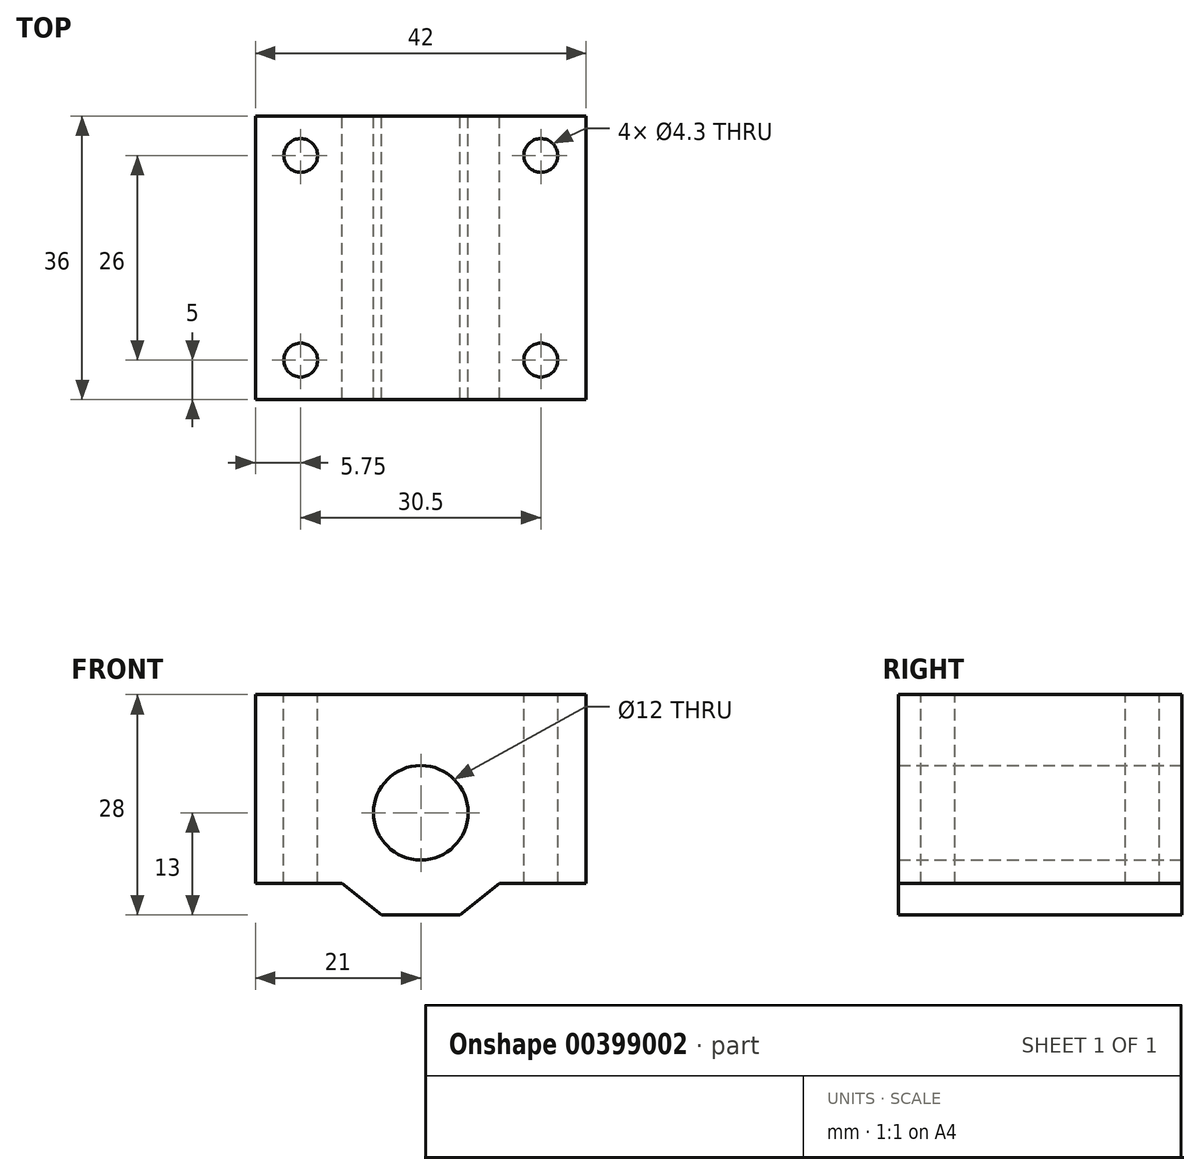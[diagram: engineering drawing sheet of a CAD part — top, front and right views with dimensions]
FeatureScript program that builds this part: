
annotation { "Feature Type Name" : "Feature", "Feature Type Description" : "" }
export const myFeature = defineFeature(function(context is Context, id is Id, definition is map)
    precondition{}
    {
        {
            var Q0;
            Q0=qCreatedBy(makeId("Front.planeOp"),FACE);
            var sketch = newSketch(context, id + "F0", { "sketchPlane" : qUnion([Q0])});
            skCircle(sketch, "E0", {"center": v(0, 0) * mm, "radius": 6 * mm});
            skLineSegment(sketch, "E1.bottom", {"start": v(-21, 15) * mm, "end": v(21, 15) * mm});
            skLineSegment(sketch, "E1.top", {"start": v(-21, -9) * mm, "end": v(-10, -9) * mm});
            skLineSegment(sketch, "E1.left", {"start": v(-21, 15) * mm, "end": v(-21, -9) * mm});
            skLineSegment(sketch, "E1.right", {"start": v(21, 15) * mm, "end": v(21, -9) * mm});
            skLineSegment(sketch, "E2", {"start": v(-10, -9) * mm, "end": v(-5, -13) * mm});
            skLineSegment(sketch, "E3", {"start": v(-5, -13) * mm, "end": v(0, -13) * mm});
            skLineSegment(sketch, "E4.MirrorCS", {"start": v(5, -13) * mm, "end": v(0, -13) * mm});
            skLineSegment(sketch, "E5.MirrorCS", {"start": v(10, -9) * mm, "end": v(5, -13) * mm});
            skLineSegment(sketch, "E6.trimOffspring", {"start": v(10, -9) * mm, "end": v(21, -9) * mm});
            skSolve(sketch);
        }
        {
            var Q0;
            Q0=makeQuery(id+"F0.imprint","IMPRINT",FACE,{"disambiguationData":[TD([[makeQuery(id+"F0.imprint","IMPRINT",EDGE,{"derivedFrom":sQuery(id+"F0.wireOp",EDGE,"E0")}),-1.0]])]});
            extrude(context, id + "F1", {"entities" : qUnion([Q0]), "depth" : 36 * mm, "hasSecondDirection" : true, "secondDirectionOppositeDirection" : true, "secondDirectionDepth" : 18 * mm, "symmetric" : true});
        }
        {
            var Q0;
            Q0=makeQuery(id+"F1.opExtrude","SWEPT_FACE",FACE,{"disambiguationData":[OSD([sQuery(id+"F0.wireOp",EDGE,"E1.bottom")])]});
            var sketch = newSketch(context, id + "F2", { "sketchPlane" : qUnion([Q0])});
            skPoint(sketch, "E7", {"position": v(-15.25, 13) * mm});
            skPoint(sketch, "E8.MirrorP", {"position": v(15.25, 13) * mm});
            skPoint(sketch, "E9.MirrorP", {"position": v(-15.25, -13) * mm});
            skPoint(sketch, "E10.MirrorP", {"position": v(15.25, -13) * mm});
            skSolve(sketch);
        }
        {
            var Q0;
            Q0=sQuery(id+"F2.wireOp",VERTEX,"E7");
            var Q1;
            Q1=sQuery(id+"F2.wireOp",VERTEX,"E8.MirrorP");
            var Q2;
            Q2=sQuery(id+"F2.wireOp",VERTEX,"E10.MirrorP");
            var Q3;
            Q3=sQuery(id+"F2.wireOp",VERTEX,"E9.MirrorP");
            var Q4;
            Q4=makeQuery(id+"F1.opExtrude","SWEPT_BODY",BODY,{"disambiguationData":[OSD([sQuery(id+"F0.wireOp",EDGE,"E0"),sQuery(id+"F0.wireOp",EDGE,"E1.bottom"),sQuery(id+"F0.wireOp",EDGE,"E1.top"),sQuery(id+"F0.wireOp",EDGE,"E1.left"),sQuery(id+"F0.wireOp",EDGE,"E1.right"),sQuery(id+"F0.wireOp",EDGE,"E2"),sQuery(id+"F0.wireOp",EDGE,"E3"),sQuery(id+"F0.wireOp",EDGE,"E4.MirrorCS"),sQuery(id+"F0.wireOp",EDGE,"E5.MirrorCS"),sQuery(id+"F0.wireOp",EDGE,"E6.trimOffspring")])]});
            hole(context, id + "F3", {"style" : HoleStyle.SIMPLE, "endStyle" : HoleEndStyle.THROUGH, "holeDiameter" : 4.3 * mm, "isTappedThrough" : true, "tappedDepth" : 3 * mm, "tapClearance" : 3, "locations" : qUnion([Q0, Q1, Q2, Q3]), "scope" : qUnion([Q4])});
        }
    });
